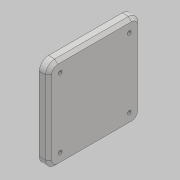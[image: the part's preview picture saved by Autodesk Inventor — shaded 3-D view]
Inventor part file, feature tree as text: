
AUTODESK INVENTOR PART (.ipt)
format: ipt  version: 2018 (Build 220112000, 112)  size: 122,880 bytes
history: native  units: mm
features: sketch x3, hole x2, other x1, extrude x1, fillet x1, chamfer x1, projected_geometry x1
ambient origin geometry x8: Origin, YZ Plane, XZ Plane, XY Plane, X Axis, Y Axis, Z Axis, Center Point
bodies: Body1 (feature_tree)
feature tree (10):
  other  "實體1"
  extrude  "擠出1"  Depth=300.0mm
  fillet  "圓角1"  Radius=300.0mm
  chamfer  "倒角1"  Distance=30.0mm
  hole  "孔1"  [1 undecoded]
  hole  "孔2"  [1 undecoded]
  sketch  "草圖1"
  sketch  "草圖2"
  sketch  "草圖3"
  projected_geometry  "投影迴路1"
note: 2 required parameter values undecoded (feature->parameter linkage not recoverable at this tier; creation-order binding heuristic only, values carry confidence <= 0.55)
